# Revit family: Sileo Design 100
name_source: partatom
category: Mechanical Equipment
units: mm (PartAtom-declared; Revit-internal decimal feet)

## family parameters
Always vertical = Yes
Classification = None
Cut with Voids When Loaded = No
Part Type = Normal
Room Calculation Point = No
Round Connector Dimension = Use Diameter
Shared = No
Work Plane-Based = No

## types (1)
- Sileo Design 100
    00_20_Manufacturer = Blauberg
    00_20_Name = Axial fan
    00_20_Type = Sileo Design 100
    Amperage = 0 A
    Apparent Load = 12 W
    B = 200 mm  [stored 0.656168 ft]
    Casing Material = Plastic, white
    D = 99 mm  [stored 0.324803 ft]
    Default Elevation = 0 mm  [stored 0 ft]
    Diameter = 99 mm  [stored 0.324803 ft]
    Dn = 103 mm  [stored 0.337927 ft]
    Frequency = 50 Hz
    Height = 200 mm  [stored 0.656168 ft]
    L = 130 mm  [stored 0.426509 ft]
    L1 = 49 mm  [stored 0.160761 ft]
    L2 = 81 mm  [stored 0.265748 ft]
    Length = 130 mm  [stored 0.426509 ft]
    Load Classification = HVAC
    Maintenance zone material = <By Category>
    Manufacturer = Blauberg
    Maximum Air Flow = 90.0 m³/h
    Number of Fase = 1
    Power = 8 W
    Pressure_Static_Air = 0.0 Pa
    Sound pressure level at 3 m distance = 26 dBA
    URL = https://blaubergventilatoren.de
    Voltage = 230 V
    Weight = 0.66 kg
    Width = 200 mm  [stored 0.656168 ft]

note: [stored X ft] marks values corroborated as IEEE doubles in the binary element streams (Revit-internal decimal feet)
